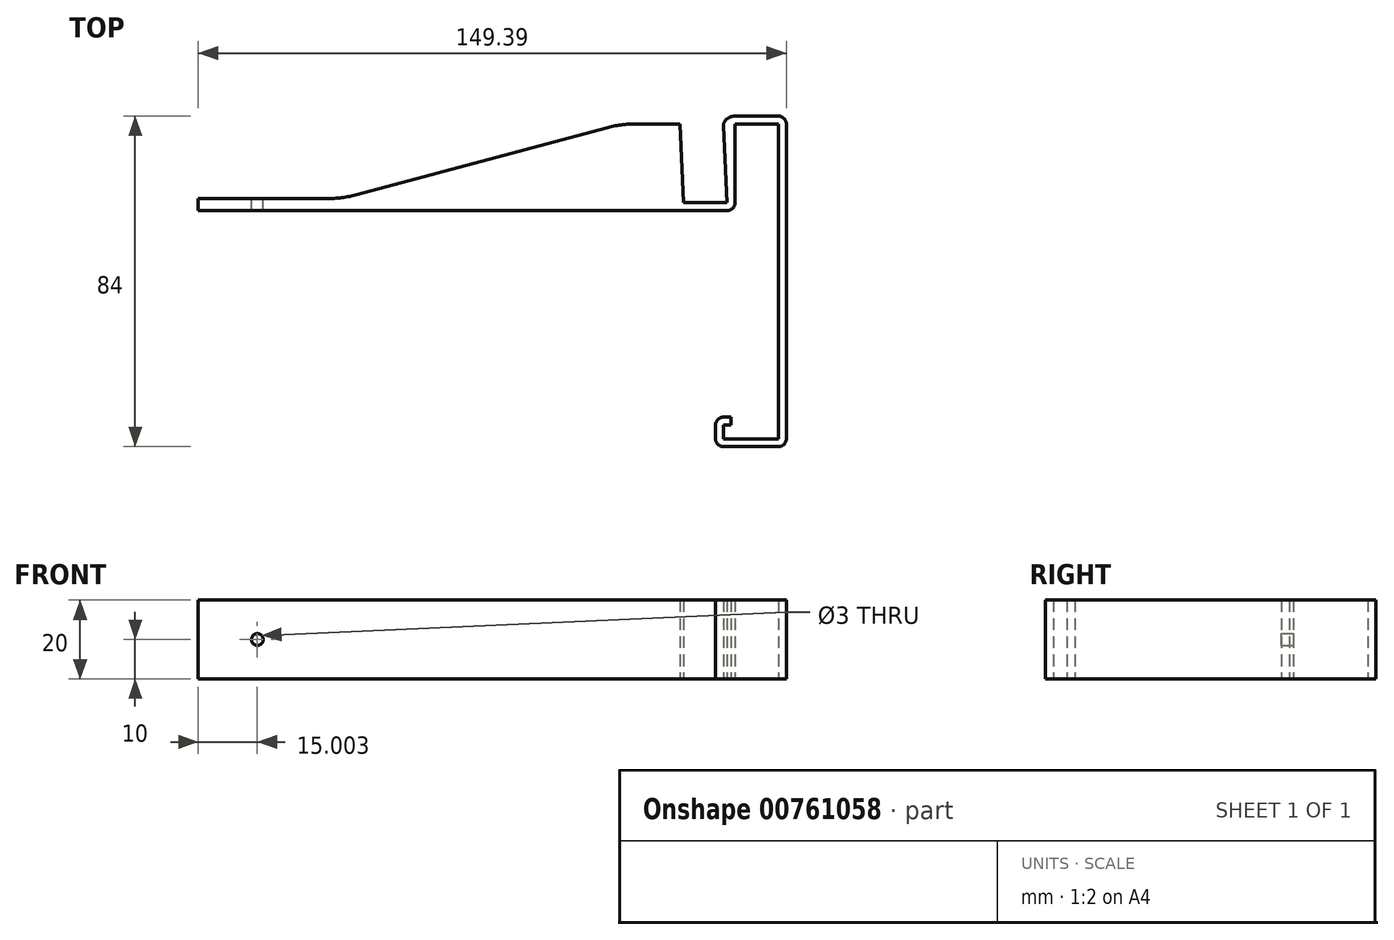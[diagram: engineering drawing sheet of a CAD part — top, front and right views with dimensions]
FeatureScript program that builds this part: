
annotation { "Feature Type Name" : "Feature", "Feature Type Description" : "" }
export const myFeature = defineFeature(function(context is Context, id is Id, definition is map)
    precondition{}
    {
        {
            var Q0;
            Q0=qCreatedBy(makeId("Top.planeOp"),FACE);
            var sketch = newSketch(context, id + "F0", { "sketchPlane" : qUnion([Q0])});
            skLineSegment(sketch, "E0", {"start": v(0, 0) * mm, "end": v(0, -3.5) * mm});
            skLineSegment(sketch, "E1", {"start": v(0, -3.5) * mm, "end": v(14, -3.5) * mm});
            skLineSegment(sketch, "E2", {"start": v(14, -3.5) * mm, "end": v(14, 54.5) * mm});
            skLineSegment(sketch, "E3", {"start": v(14, 54.5) * mm, "end": v(14, 76.5) * mm});
            skLineSegment(sketch, "E4", {"start": v(14, 76.5) * mm, "end": v(3, 76.5) * mm});
            skLineSegment(sketch, "E5", {"start": v(0, 76.5) * mm, "end": v(0.9, 56.5) * mm});
            skLineSegment(sketch, "E6", {"start": v(1, 54.5) * mm, "end": v(-10, 54.5) * mm});
            skLineSegment(sketch, "E7", {"start": v(-10.1, 56.5) * mm, "end": v(-11, 76.5) * mm});
            skLineSegment(sketch, "E8", {"start": v(-11, 76.5) * mm, "end": v(-26, 76.5) * mm});
            skLineSegment(sketch, "E9", {"start": v(-10, 54.5) * mm, "end": v(-133.39, 54.5) * mm});
            skLineSegment(sketch, "E10", {"start": v(-133.39, 54.5) * mm, "end": v(-133.39, 57.5) * mm});
            skLineSegment(sketch, "E11", {"start": v(-133.39, 57.5) * mm, "end": v(-96.9, 57.5) * mm});
            skLineSegment(sketch, "E12", {"start": v(-26, 76.5) * mm, "end": v(-96.9, 57.5) * mm});
            skLineSegment(sketch, "E13", {"start": v(0.9, 56.5) * mm, "end": v(-10.1, 56.5) * mm});
            skLineSegment(sketch, "E14.0", {"start": v(14, 78.5) * mm, "end": v(3, 78.5) * mm});
            skLineSegment(sketch, "E15.0", {"start": v(16, 54.5) * mm, "end": v(16, 76.5) * mm});
            skLineSegment(sketch, "E15.1", {"start": v(16, -5.5) * mm, "end": v(16, 54.5) * mm});
            skLineSegment(sketch, "E15.2", {"start": v(-2, -5.5) * mm, "end": v(16, -5.5) * mm});
            skLineSegment(sketch, "E15.3", {"start": v(-2, 0) * mm, "end": v(-2, -5.5) * mm});
            skArc(sketch, "E16", {"start": v(16, 76.5) * mm, "mid": v(15.41, 77.91) * mm, "end": v(14, 78.5) * mm});
            skLineSegment(sketch, "E17", {"start": v(-2, 0) * mm, "end": v(-2, 2) * mm});
            skLineSegment(sketch, "E18", {"start": v(-2, 2) * mm, "end": v(2, 2) * mm});
            skLineSegment(sketch, "E19", {"start": v(2, 2) * mm, "end": v(2, 0) * mm});
            skLineSegment(sketch, "E20", {"start": v(2, 0) * mm, "end": v(0, 0) * mm});
            skLineSegment(sketch, "E21", {"start": v(1, 54.5) * mm, "end": v(3, 54.5) * mm});
            skLineSegment(sketch, "E22", {"start": v(3, 54.5) * mm, "end": v(3, 76.5) * mm});
            skArc(sketch, "E23", {"start": v(3, 78.5) * mm, "mid": v(1.2, 77.95) * mm, "end": v(0, 76.5) * mm});
            skSolve(sketch);
        }
        {
            var Q0;
            Q0=makeQuery(id+"F0.imprint","IMPRINT",FACE,{"disambiguationData":[TD([[makeQuery(id+"F0.imprint","IMPRINT",EDGE,{"derivedFrom":sQuery(id+"F0.wireOp",EDGE,"E0")}),-1.0]])]});
            extrude(context, id + "F1", {"entities" : qUnion([Q0]), "depth" : 20 * mm, "offsetDistance" : 25 * mm});
        }
        {
            var Q0;
            Q0=makeQuery(id+"F1.opExtrude","SWEPT_EDGE",EDGE,{"disambiguationData":[OSD([sQuery(id+"F0.wireOp",EDGE,"E11"),sQuery(id+"F0.wireOp",EDGE,"E12")])]});
            var Q1;
            Q1=makeQuery(id+"F1.opExtrude","SWEPT_EDGE",EDGE,{"disambiguationData":[OSD([sQuery(id+"F0.wireOp",EDGE,"E8"),sQuery(id+"F0.wireOp",EDGE,"E12")])]});
            fillet(context, id + "F2", {"entities" : qUnion([Q0, Q1]), "radius" : 30 * mm, "tangentPropagation" : true, "allowEdgeOverflow" : false});
        }
        {
            var Q0;
            Q0=makeQuery(id+"F1.opExtrude","SWEPT_EDGE",EDGE,{"disambiguationData":[OSD([sQuery(id+"F0.wireOp",EDGE,"E5"),sQuery(id+"F0.wireOp",EDGE,"E23")])]});
            fillet(context, id + "F3", {"entities" : qUnion([Q0]), "radius" : 2 * mm, "tangentPropagation" : true, "allowEdgeOverflow" : false});
        }
        {
            var Q0;
            Q0=makeQuery(id+"F1.opExtrude","SWEPT_EDGE",EDGE,{"disambiguationData":[OSD([sQuery(id+"F0.wireOp",EDGE,"E15.1"),sQuery(id+"F0.wireOp",EDGE,"E15.2")])]});
            var Q1;
            Q1=makeQuery(id+"F1.opExtrude","SWEPT_EDGE",EDGE,{"disambiguationData":[OSD([sQuery(id+"F0.wireOp",EDGE,"E15.2"),sQuery(id+"F0.wireOp",EDGE,"E15.3")])]});
            var Q2;
            Q2=makeQuery(id+"F1.opExtrude","SWEPT_EDGE",EDGE,{"disambiguationData":[OSD([sQuery(id+"F0.wireOp",EDGE,"E17"),sQuery(id+"F0.wireOp",EDGE,"E18")])]});
            var Q3;
            Q3=makeQuery(id+"F1.opExtrude","SWEPT_EDGE",EDGE,{"disambiguationData":[OSD([sQuery(id+"F0.wireOp",EDGE,"E21"),sQuery(id+"F0.wireOp",EDGE,"E22")])]});
            fillet(context, id + "F4", {"entities" : qUnion([Q0, Q1, Q2, Q3]), "radius" : 2 * mm, "tangentPropagation" : true, "allowEdgeOverflow" : false});
        }
        {
            var Q0;
            Q0=makeQuery(id+"F1.opExtrude","SWEPT_FACE",FACE,{"disambiguationData":[OSD([sQuery(id+"F0.wireOp",EDGE,"E11")])]});
            var sketch = newSketch(context, id + "F5", { "sketchPlane" : qUnion([Q0])});
            skCircle(sketch, "E24", {"center": v(118.39, 10) * mm, "radius": 1.5 * mm});
            skSolve(sketch);
        }
        {
            var Q0;
            Q0=makeQuery(id+"F5.imprint","IMPRINT",FACE,{"disambiguationData":[TD([[makeQuery(id+"F5.imprint","IMPRINT",EDGE,{"derivedFrom":sQuery(id+"F5.wireOp",EDGE,"E24")}),1.0]])]});
            extrude(context, id + "F6", {"entities" : qUnion([Q0]), "operationType" : NewBodyOperationType.REMOVE, "oppositeDirection" : true, "depth" : 25 * mm, "offsetDistance" : 25 * mm});
        }
    });
